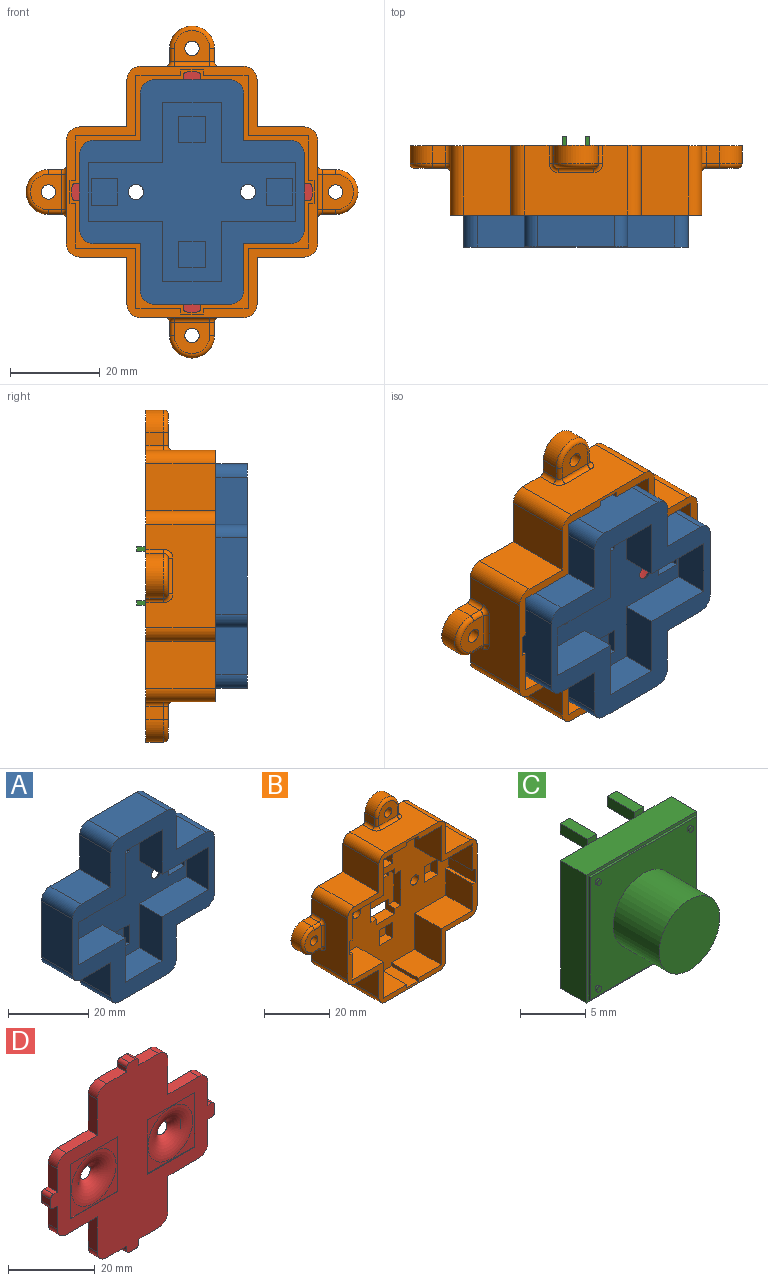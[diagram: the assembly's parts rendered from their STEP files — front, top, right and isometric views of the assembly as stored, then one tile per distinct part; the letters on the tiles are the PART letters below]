
ASSEMBLY  parts=4 mates=3
PART A: 67 faces, bbox 50x11x50 mm
  f0: plane 46x40mm, normal (0,-1,0), area 796.3mm2, adj f14,f15,f16,f17,f18,f19,f20,f21
  f1: plane 50x50mm, normal (0,1,0), area 1281.2mm2, adj f2,f3,f4,f5,f6,f7,f8,f9
  f2: plane 11x10.5mm, normal (0,0,1), area 115.5mm2, adj f1,f13,f26,f27
  f3: plane 17x11mm, normal (-1,0,0), area 187mm2, adj f1,f26,f27,f28
  f4: plane 11x10.5mm, normal (0,0,-1), area 115.5mm2, adj f1,f5,f26,f28
  f5: plane 11x10.5mm, normal (-1,0,0), area 115.5mm2, adj f1,f4,f26,f29
  f6: plane 17x11mm, normal (0,0,-1), area 187mm2, adj f1,f26,f29,f30
  f7: plane 11x10.5mm, normal (1,0,0), area 115.5mm2, adj f1,f8,f26,f30
  f8: plane 11x10.5mm, normal (0,0,-1), area 115.5mm2, adj f1,f7,f26,f31
  f9: plane 17x11mm, normal (1,0,0), area 187mm2, adj f1,f26,f31,f32
  f10: plane 11x10.5mm, normal (0,0,1), area 115.5mm2, adj f1,f11,f26,f32
  f11: plane 11x10.5mm, normal (1,0,0), area 115.5mm2, adj f1,f10,f26,f33
  f12: plane 17x11mm, normal (0,0,1), area 187mm2, adj f1,f26,f33,f34
  f13: plane 11x10.5mm, normal (-1,0,0), area 115.5mm2, adj f1,f2,f26,f34
  f14: plane 13.5x8mm, normal (1,0,0), area 108mm2, adj f0,f15,f25,f26
  f15: plane 13x8mm, normal (0,0,-1), area 104mm2, adj f0,f14,f16,f26
  f16: plane 13.5x8mm, normal (-1,0,0), area 108mm2, adj f0,f15,f17,f26
  f17: plane 16.5x8mm, normal (0,0,-1), area 132mm2, adj f0,f16,f18,f26
  f18: plane 13x8mm, normal (-1,0,0), area 104mm2, adj f0,f17,f19,f26
  f19: plane 16.5x8mm, normal (0,0,1), area 132mm2, adj f0,f18,f20,f26
  f20: plane 13.5x8mm, normal (-1,0,0), area 108mm2, adj f0,f19,f21,f26
  f21: plane 13x8mm, normal (0,0,1), area 104mm2, adj f0,f20,f22,f26
  f22: plane 13.5x8mm, normal (1,0,0), area 108mm2, adj f0,f21,f23,f26
  f23: plane 16.5x8mm, normal (0,0,1), area 132mm2, adj f0,f22,f24,f26
  f24: plane 13x8mm, normal (1,0,0), area 104mm2, adj f0,f23,f25,f26
  f25: plane 16.5x8mm, normal (0,0,-1), area 132mm2, adj f0,f14,f24,f26
  f26: plane 50x50mm, normal (0,-1,0), area 806.5mm2, adj f2,f3,f4,f5,f6,f7,f8,f9
  f27: cylinder r=3mm len=11mm, axis (0,1,0), area 51.8mm2, adj f1,f2,f3,f26
  f28: cylinder r=3mm len=11mm, axis (0,1,0), area 51.8mm2, adj f1,f3,f4,f26
  f29: cylinder r=3mm len=11mm, axis (0,1,0), area 51.8mm2, adj f1,f5,f6,f26
  f30: cylinder r=3mm len=11mm, axis (0,1,0), area 51.8mm2, adj f1,f6,f7,f26
  f31: cylinder r=3mm len=11mm, axis (0,1,0), area 51.8mm2, adj f1,f8,f9,f26
  f32: cylinder r=3mm len=11mm, axis (0,1,0), area 51.8mm2, adj f1,f9,f10,f26
  f33: cylinder r=3mm len=11mm, axis (0,1,0), area 51.8mm2, adj f1,f11,f12,f26
  f34: cylinder r=3mm len=11mm, axis (0,1,0), area 51.8mm2, adj f1,f12,f13,f26
  f35: plane 15.4x0.2mm, normal (0,0,-1), area 3.1mm2, adj f1,f36,f38,f39
  f36: plane 15.4x0.2mm, normal (-1,0,0), area 3.1mm2, adj f1,f35,f37,f39
  f37: plane 15.4x0.2mm, normal (0,0,1), area 3.1mm2, adj f1,f36,f38,f39
  f38: plane 15.4x0.2mm, normal (1,0,0), area 3.1mm2, adj f1,f35,f37,f39
  f39: plane 15.4x15.4mm, normal (0,1,0), area 69.7mm2, adj f35,f36,f37,f38,f65
  f40: plane 15.4x0.2mm, normal (0,0,-1), area 3.1mm2, adj f1,f41,f43,f44
  f41: plane 15.4x0.2mm, normal (-1,0,0), area 3.1mm2, adj f1,f40,f42,f44
  f42: plane 15.4x0.2mm, normal (0,0,1), area 3.1mm2, adj f1,f41,f43,f44
  f43: plane 15.4x0.2mm, normal (1,0,0), area 3.1mm2, adj f1,f40,f42,f44
  f44: plane 15.4x15.4mm, normal (0,1,0), area 69.7mm2, adj f40,f41,f42,f43,f66
  f45: plane 5.8x2mm, normal (0,0,1), area 11.6mm2, adj f0,f46,f48,f49
  f46: plane 5.8x2mm, normal (-1,0,0), area 11.6mm2, adj f0,f45,f47,f49
  f47: plane 5.8x2mm, normal (0,0,-1), area 11.6mm2, adj f0,f46,f48,f49
  f48: plane 5.8x2mm, normal (1,0,0), area 11.6mm2, adj f0,f45,f47,f49
  f49: plane 5.8x5.8mm, normal (0,-1,0), area 33.6mm2, adj f45,f46,f47,f48
  f50: plane 5.8x2mm, normal (-1,0,0), area 11.6mm2, adj f0,f51,f53,f54
  f51: plane 5.8x2mm, normal (0,0,-1), area 11.6mm2, adj f0,f50,f52,f54
  f52: plane 5.8x2mm, normal (1,0,0), area 11.6mm2, adj f0,f51,f53,f54
  f53: plane 5.8x2mm, normal (0,0,1), area 11.6mm2, adj f0,f50,f52,f54
  f54: plane 5.8x5.8mm, normal (0,-1,0), area 33.6mm2, adj f50,f51,f52,f53
  f55: plane 5.8x2mm, normal (0,0,-1), area 11.6mm2, adj f0,f56,f58,f59
  f56: plane 5.8x2mm, normal (1,0,0), area 11.6mm2, adj f0,f55,f57,f59
  f57: plane 5.8x2mm, normal (0,0,1), area 11.6mm2, adj f0,f56,f58,f59
  f58: plane 5.8x2mm, normal (-1,0,0), area 11.6mm2, adj f0,f55,f57,f59
  f59: plane 5.8x5.8mm, normal (0,-1,0), area 33.6mm2, adj f55,f56,f57,f58
  f60: plane 5.8x2mm, normal (0,0,1), area 11.6mm2, adj f0,f61,f63,f64
  f61: plane 5.8x2mm, normal (-1,0,0), area 11.6mm2, adj f0,f60,f62,f64
  f62: plane 5.8x2mm, normal (0,0,-1), area 11.6mm2, adj f0,f61,f63,f64
  f63: plane 5.8x2mm, normal (1,0,0), area 11.6mm2, adj f0,f60,f62,f64
  f64: plane 5.8x5.8mm, normal (0,-1,0), area 33.6mm2, adj f60,f61,f62,f63
  f65: torus R=7.3mm, axis (0,1,0), area 174.6mm2, adj f0,f39
  f66: torus R=7.3mm, axis (0,1,0), area 174.6mm2, adj f0,f44
PART B: 140 faces, bbox 74.8x15.5x74.8 mm
  f0: plane 11.5x10mm, normal (0,0,-1), area 115mm2, adj f4,f5,f58,f79
  f1: plane 11.5x10mm, normal (-1,0,0), area 115mm2, adj f4,f5,f61,f69
  f2: plane 11.5x10mm, normal (0,0,1), area 115mm2, adj f4,f5,f64,f71
  f3: plane 11.5x10mm, normal (1,0,0), area 115mm2, adj f4,f5,f67,f74
  f4: plane 56x56mm, normal (0,-1,0), area 392.5mm2, adj f0,f1,f2,f3,f11,f12,f13,f14
  f5: plane 54.4x54.4mm, normal (0,-1,0), area 1645.3mm2, adj f0,f1,f2,f3,f7,f9,f23,f24
  f6: plane 8x1mm, normal (0,0,-1), area 8mm2, adj f10,f25,f27,f35
  f7: plane 4x4mm, normal (1,0,0), area 10mm2, adj f5,f8,f10,f28,f32,f35
  f8: plane 8x1mm, normal (0,0,1), area 8mm2, adj f7,f9,f10,f35
  f9: plane 4x4mm, normal (-1,0,0), area 10mm2, adj f5,f8,f10,f28,f31,f35
  f10: plane 74x74mm, normal (0,1,0), area 2596mm2, adj f6,f7,f8,f9,f11,f12,f13,f14
  f11: plane 23x15.5mm, normal (-1,0,0), area 286.2mm2, adj f4,f10,f80,f83,f124,f126,f128,f130
  f12: plane 15.5x10.5mm, normal (0,0,-1), area 162.8mm2, adj f4,f10,f13,f80
  f13: plane 15.5x10.5mm, normal (-1,0,0), area 162.8mm2, adj f4,f10,f12,f81
  f14: plane 23x15.5mm, normal (0,0,-1), area 286.2mm2, adj f4,f10,f81,f84,f116,f118,f120,f122
  f15: plane 15.5x10.5mm, normal (1,0,0), area 162.8mm2, adj f4,f10,f16,f84
  f16: plane 15.5x10.5mm, normal (0,0,-1), area 162.8mm2, adj f4,f10,f15,f85
  f17: plane 23x15.5mm, normal (1,0,0), area 286.2mm2, adj f4,f10,f85,f86,f108,f110,f112,f114
  f18: plane 15.5x10.5mm, normal (0,0,1), area 162.8mm2, adj f4,f10,f19,f86
  f19: plane 15.5x10.5mm, normal (1,0,0), area 162.7mm2, adj f4,f10,f18,f87
  f20: plane 23x15.5mm, normal (0,0,1), area 286.2mm2, adj f4,f10,f82,f87,f132,f134,f136,f138
  f21: plane 15.5x10.5mm, normal (-1,0,0), area 162.7mm2, adj f4,f10,f22,f82
  f22: plane 15.5x10.5mm, normal (0,0,1), area 162.8mm2, adj f4,f10,f21,f83
  f23: cylinder r=1.7mm len=4mm, axis (0,1,0), area 42.7mm2, adj f5,f10
  f24: cylinder r=1.7mm len=4mm, axis (0,1,0), area 42.7mm2, adj f5,f10
  f25: plane 4x4mm, normal (1,0,0), area 10mm2, adj f5,f6,f10,f26,f34,f35
  f26: plane 8x4mm, normal (0,0,1), area 32mm2, adj f5,f10,f25,f27
  f27: plane 4x4mm, normal (-1,0,0), area 10mm2, adj f5,f6,f10,f26,f29,f35
  f28: plane 8x4mm, normal (0,0,-1), area 32mm2, adj f5,f7,f9,f10
  f29: plane 3x2.5mm, normal (0,0,1), area 7.5mm2, adj f5,f27,f30,f35
  f30: plane 13x3mm, normal (-1,0,0), area 39mm2, adj f5,f29,f31,f35
  f31: plane 3x2.5mm, normal (0,0,-1), area 7.5mm2, adj f5,f9,f30,f35
  f32: plane 3x2.5mm, normal (0,0,-1), area 7.5mm2, adj f5,f7,f33,f35
  f33: plane 13x3mm, normal (1,0,0), area 39mm2, adj f5,f32,f34,f35
  f34: plane 3x2.5mm, normal (0,0,1), area 7.5mm2, adj f5,f25,f33,f35
  f35: plane 13x13mm, normal (0,-1,0), area 137mm2, adj f6,f7,f8,f9,f25,f27,f29,f30
  f36: plane 5.8x3mm, normal (1,0,0), area 17.4mm2, adj f5,f37,f39,f40
  f37: plane 5.8x3mm, normal (0,0,1), area 17.4mm2, adj f5,f36,f38,f40
  f38: plane 5.8x3mm, normal (-1,0,0), area 17.4mm2, adj f5,f37,f39,f40
  f39: plane 5.8x3mm, normal (0,0,-1), area 17.4mm2, adj f5,f36,f38,f40
  f40: plane 5.8x5.8mm, normal (0,-1,0), area 33.6mm2, adj f36,f37,f38,f39
  f41: plane 5.8x3mm, normal (0,0,-1), area 17.4mm2, adj f5,f42,f44,f45
  f42: plane 5.8x3mm, normal (1,0,0), area 17.4mm2, adj f5,f41,f43,f45
  f43: plane 5.8x3mm, normal (0,0,1), area 17.4mm2, adj f5,f42,f44,f45
  f44: plane 5.8x3mm, normal (-1,0,0), area 17.4mm2, adj f5,f41,f43,f45
  f45: plane 5.8x5.8mm, normal (0,-1,0), area 33.6mm2, adj f41,f42,f43,f44
  f46: plane 5.8x3mm, normal (0,0,-1), area 17.4mm2, adj f5,f47,f49,f50
  f47: plane 5.8x3mm, normal (1,0,0), area 17.4mm2, adj f5,f46,f48,f50
  f48: plane 5.8x3mm, normal (0,0,1), area 17.4mm2, adj f5,f47,f49,f50
  f49: plane 5.8x3mm, normal (-1,0,0), area 17.4mm2, adj f5,f46,f48,f50
  f50: plane 5.8x5.8mm, normal (0,-1,0), area 33.6mm2, adj f46,f47,f48,f49
  f51: plane 5.8x3mm, normal (-1,0,0), area 17.4mm2, adj f5,f52,f54,f55
  f52: plane 5.8x3mm, normal (0,0,-1), area 17.4mm2, adj f5,f51,f53,f55
  f53: plane 5.8x3mm, normal (1,0,0), area 17.4mm2, adj f5,f52,f54,f55
  f54: plane 5.8x3mm, normal (0,0,1), area 17.4mm2, adj f5,f51,f53,f55
  f55: plane 5.8x5.8mm, normal (0,-1,0), area 33.6mm2, adj f51,f52,f53,f54
  f56: plane 13.5x11.5mm, normal (1,0,0), area 155.2mm2, adj f4,f5,f57,f67
  f57: plane 11.5x10mm, normal (0,0,-1), area 115mm2, adj f4,f5,f56,f78
  f58: plane 13.5x11.5mm, normal (-1,0,0), area 155.2mm2, adj f0,f4,f5,f59
  f59: plane 13.5x11.5mm, normal (0,0,-1), area 155.3mm2, adj f4,f5,f58,f60
  f60: plane 11.5x10mm, normal (-1,0,0), area 115mm2, adj f4,f5,f59,f68
  f61: plane 13.5x11.5mm, normal (0,0,1), area 155.3mm2, adj f1,f4,f5,f62
  f62: plane 13.5x11.5mm, normal (-1,0,0), area 155.2mm2, adj f4,f5,f61,f63
  f63: plane 11.5x10mm, normal (0,0,1), area 115mm2, adj f4,f5,f62,f73
  f64: plane 13.5x11.5mm, normal (1,0,0), area 155.2mm2, adj f2,f4,f5,f65
  f65: plane 13.5x11.5mm, normal (0,0,1), area 155.3mm2, adj f4,f5,f64,f66
  f66: plane 11.5x10mm, normal (1,0,0), area 115mm2, adj f4,f5,f65,f76
  f67: plane 13.5x11.5mm, normal (0,0,-1), area 155.3mm2, adj f3,f4,f5,f56
  f68: plane 11.5x1.2mm, normal (0,0,-1), area 13.8mm2, adj f4,f5,f60,f70
  f69: plane 11.5x1.2mm, normal (0,0,1), area 13.8mm2, adj f1,f4,f5,f70
  f70: plane 11.5x5mm, normal (-1,0,0), area 57.5mm2, adj f4,f5,f68,f69
  f71: plane 11.5x1.2mm, normal (1,0,0), area 13.8mm2, adj f2,f4,f5,f72
  f72: plane 11.5x5mm, normal (0,0,1), area 57.5mm2, adj f4,f5,f71,f73
  f73: plane 11.5x1.2mm, normal (-1,0,0), area 13.8mm2, adj f4,f5,f63,f72
  f74: plane 11.5x1.2mm, normal (0,0,-1), area 13.8mm2, adj f3,f4,f5,f75
  f75: plane 11.5x5mm, normal (1,0,0), area 57.5mm2, adj f4,f5,f74,f76
  f76: plane 11.5x1.2mm, normal (0,0,1), area 13.8mm2, adj f4,f5,f66,f75
  f77: plane 11.5x5mm, normal (0,0,-1), area 57.5mm2, adj f4,f5,f78,f79
  f78: plane 11.5x1.2mm, normal (1,0,0), area 13.8mm2, adj f4,f5,f57,f77
  f79: plane 11.5x1.2mm, normal (-1,0,0), area 13.8mm2, adj f0,f4,f5,f77
  f80: cylinder r=3mm len=15.5mm, axis (0,1,0), area 73mm2, adj f4,f10,f11,f12
  f81: cylinder r=3mm len=15.5mm, axis (0,1,0), area 73mm2, adj f4,f10,f13,f14
  f82: cylinder r=3mm len=15.5mm, axis (0,1,0), area 73mm2, adj f4,f10,f20,f21
  f83: cylinder r=3mm len=15.5mm, axis (0,1,0), area 73mm2, adj f4,f10,f11,f22
  f84: cylinder r=3mm len=15.5mm, axis (0,1,0), area 73mm2, adj f4,f10,f14,f15
  f85: cylinder r=3mm len=15.5mm, axis (0,1,0), area 73mm2, adj f4,f10,f16,f17
  f86: cylinder r=3mm len=15.5mm, axis (0,1,0), area 73mm2, adj f4,f10,f17,f18
  f87: cylinder r=3mm len=15.5mm, axis (0,1,0), area 73mm2, adj f4,f10,f19,f20
  f88: plane 4x3mm, normal (0,0,1), area 12mm2, adj f10,f89,f129,f131
  f89: cylinder r=5mm len=10mm, axis (0,1,0), area 62.8mm2, adj f10,f88,f90,f127
  f90: plane 4x3mm, normal (0,0,-1), area 12mm2, adj f10,f89,f124,f125
  f91: cylinder r=1.6mm len=5mm, axis (0,1,0), area 50.3mm2, adj f10,f92
  f92: plane 8x7mm, normal (0,-1,0), area 41.1mm2, adj f91,f125,f127,f128,f129
  f93: plane 4x3mm, normal (-1,0,0), area 12mm2, adj f10,f94,f121,f123
  f94: cylinder r=5mm len=10mm, axis (0,1,0), area 62.8mm2, adj f10,f93,f95,f119
  f95: plane 4x3mm, normal (1,0,0), area 12mm2, adj f10,f94,f116,f117
  f96: cylinder r=1.6mm len=5mm, axis (0,1,0), area 50.3mm2, adj f10,f97
  f97: plane 8x7mm, normal (0,-1,0), area 41.1mm2, adj f96,f117,f119,f120,f121
  f98: plane 4x3mm, normal (0,0,-1), area 12mm2, adj f10,f99,f113,f115
  f99: cylinder r=5mm len=10mm, axis (0,1,0), area 62.8mm2, adj f10,f98,f100,f111
  f100: plane 4x3mm, normal (0,0,1), area 12mm2, adj f10,f99,f108,f109
  f101: cylinder r=1.6mm len=5mm, axis (0,1,0), area 50.3mm2, adj f10,f102
  f102: plane 8x7mm, normal (0,-1,0), area 41.1mm2, adj f101,f109,f111,f112,f113
  f103: plane 4x3mm, normal (1,0,0), area 12mm2, adj f10,f104,f137,f139
  f104: cylinder r=5mm len=10mm, axis (0,1,0), area 62.8mm2, adj f10,f103,f105,f135
  f105: plane 4x3mm, normal (-1,0,0), area 12mm2, adj f10,f104,f132,f133
  f106: cylinder r=1.6mm len=5mm, axis (0,1,0), area 50.3mm2, adj f10,f107
  f107: plane 8x7mm, normal (0,-1,0), area 41.1mm2, adj f106,f133,f135,f136,f137
  f108: cylinder r=1mm len=4mm, axis (0,-1,0), area 6.3mm2, adj f10,f17,f100,f110
  f109: cylinder r=1mm len=3mm, axis (1,0,0), area 4.7mm2, adj f100,f102,f110,f111
  f110: torus R=2mm, axis (-1,0,0), area 3.4mm2, adj f17,f108,f109,f112
  f111: torus R=4mm, axis (0,-1,0), area 22.9mm2, adj f99,f102,f109,f113
  f112: cylinder r=1mm len=8mm, axis (0,0,1), area 12.6mm2, adj f17,f102,f110,f114
  f113: cylinder r=1mm len=3mm, axis (-1,0,0), area 4.7mm2, adj f98,f102,f111,f114
  f114: torus R=2mm, axis (-1,0,0), area 3.4mm2, adj f17,f112,f113,f115
  f115: cylinder r=1mm len=4mm, axis (0,1,0), area 6.3mm2, adj f10,f17,f98,f114
  f116: cylinder r=1mm len=4mm, axis (0,-1,0), area 6.3mm2, adj f10,f14,f95,f118
  f117: cylinder r=1mm len=3mm, axis (0,0,-1), area 4.7mm2, adj f95,f97,f118,f119
  f118: torus R=2mm, axis (0,0,1), area 3.4mm2, adj f14,f116,f117,f120
  f119: torus R=4mm, axis (0,-1,0), area 22.9mm2, adj f94,f97,f117,f121
  f120: cylinder r=1mm len=8mm, axis (1,0,0), area 12.6mm2, adj f14,f97,f118,f122
  f121: cylinder r=1mm len=3mm, axis (0,0,1), area 4.7mm2, adj f93,f97,f119,f122
  f122: torus R=2mm, axis (0,0,1), area 3.4mm2, adj f14,f120,f121,f123
  f123: cylinder r=1mm len=4mm, axis (0,1,0), area 6.3mm2, adj f10,f14,f93,f122
  f124: cylinder r=1mm len=4mm, axis (0,-1,0), area 6.3mm2, adj f10,f11,f90,f126
  f125: cylinder r=1mm len=3mm, axis (-1,0,0), area 4.7mm2, adj f90,f92,f126,f127
  f126: torus R=2mm, axis (1,0,0), area 3.4mm2, adj f11,f124,f125,f128
  f127: torus R=4mm, axis (0,-1,0), area 22.9mm2, adj f89,f92,f125,f129
  f128: cylinder r=1mm len=8mm, axis (0,0,-1), area 12.6mm2, adj f11,f92,f126,f130
  f129: cylinder r=1mm len=3mm, axis (1,0,0), area 4.7mm2, adj f88,f92,f127,f130
  f130: torus R=2mm, axis (1,0,0), area 3.4mm2, adj f11,f128,f129,f131
  f131: cylinder r=1mm len=4mm, axis (0,1,0), area 6.3mm2, adj f10,f11,f88,f130
  f132: cylinder r=1mm len=4mm, axis (0,-1,0), area 6.3mm2, adj f10,f20,f105,f134
  f133: cylinder r=1mm len=3mm, axis (0,0,1), area 4.7mm2, adj f105,f107,f134,f135
  f134: torus R=2mm, axis (0,0,-1), area 3.4mm2, adj f20,f132,f133,f136
  f135: torus R=4mm, axis (0,-1,0), area 22.9mm2, adj f104,f107,f133,f137
  f136: cylinder r=1mm len=8mm, axis (-1,0,0), area 12.6mm2, adj f20,f107,f134,f138
  f137: cylinder r=1mm len=3mm, axis (0,0,-1), area 4.7mm2, adj f103,f107,f135,f138
  f138: torus R=2mm, axis (0,0,-1), area 3.4mm2, adj f20,f136,f137,f139
  f139: cylinder r=1mm len=4mm, axis (0,1,0), area 6.3mm2, adj f10,f20,f103,f138
PART C: 45 faces, bbox 12x11x13 mm
  f0: plane 12x12mm, normal (0,1,0), area 142mm2, adj f17,f18,f19,f20,f22,f23,f24,f27
  f1: plane 11.5x11.5mm, normal (0,-1,0), area 97.3mm2, adj f2,f4,f6,f8,f10,f12,f13,f14
  f2: cylinder r=3.3mm len=6.6mm, axis (0,1,0), area 103.7mm2, adj f1,f3
  f3: plane 6.6x6.6mm, normal (0,-1,0), area 34.2mm2, adj f2
  f4: cylinder r=0.25mm len=0.5mm, axis (0,1,0), area 0.3mm2, adj f1,f5
  f5: plane 0.5x0.5mm, normal (0,-1,0), area 0.2mm2, adj f4
  f6: cylinder r=0.25mm len=0.5mm, axis (0,1,0), area 0.3mm2, adj f1,f7
  f7: plane 0.5x0.5mm, normal (0,-1,0), area 0.2mm2, adj f6
  f8: cylinder r=0.25mm len=0.5mm, axis (0,1,0), area 0.3mm2, adj f1,f9
  f9: plane 0.5x0.5mm, normal (0,-1,0), area 0.2mm2, adj f8
  f10: cylinder r=0.25mm len=0.5mm, axis (0,1,0), area 0.3mm2, adj f1,f11
  f11: plane 0.5x0.5mm, normal (0,-1,0), area 0.2mm2, adj f10
  f12: plane 11.5x0.2mm, normal (-1,0,0), area 2.3mm2, adj f1,f13,f15,f16
  f13: plane 11.5x0.2mm, normal (0,0,1), area 2.3mm2, adj f1,f12,f14,f16
  f14: plane 11.5x0.2mm, normal (1,0,0), area 2.3mm2, adj f1,f13,f15,f16
  f15: plane 11.5x0.2mm, normal (0,0,-1), area 2.3mm2, adj f1,f12,f14,f16
  f16: plane 12x12mm, normal (0,-1,0), area 11.8mm2, adj f12,f13,f14,f15,f17,f18,f19,f20
  f17: plane 12x2.8mm, normal (-1,0,0), area 33.6mm2, adj f0,f16,f18,f20
  f18: plane 12x2.8mm, normal (0,0,1), area 33.6mm2, adj f0,f16,f17,f19,f26,f32
  f19: plane 12x2.8mm, normal (1,0,0), area 33.6mm2, adj f0,f16,f18,f20
  f20: plane 12x2.8mm, normal (0,0,-1), area 33.6mm2, adj f0,f16,f17,f19,f33,f39
  f21: plane 3x1mm, normal (0,0,1), area 3mm2, adj f22,f24,f25,f26
  f22: plane 3x1mm, normal (1,0,0), area 3mm2, adj f0,f21,f23,f25,f26
  f23: plane 3x1mm, normal (0,0,-1), area 3mm2, adj f0,f22,f24,f25
  f24: plane 3x1mm, normal (-1,0,0), area 3mm2, adj f0,f21,f23,f25,f26
  f25: plane 1x1mm, normal (0,1,0), area 1mm2, adj f21,f22,f23,f24
  f26: plane 1x0.5mm, normal (0,-1,0), area 0.5mm2, adj f18,f21,f22,f24
  f27: plane 3x1mm, normal (0,0,-1), area 3mm2, adj f0,f28,f30,f31
  f28: plane 3x1mm, normal (-1,0,0), area 3mm2, adj f0,f27,f29,f31,f32
  f29: plane 3x1mm, normal (0,0,1), area 3mm2, adj f28,f30,f31,f32
  f30: plane 3x1mm, normal (1,0,0), area 3mm2, adj f0,f27,f29,f31,f32
  f31: plane 1x1mm, normal (0,1,0), area 1mm2, adj f27,f28,f29,f30
  f32: plane 1x0.5mm, normal (0,-1,0), area 0.5mm2, adj f18,f28,f29,f30
  f33: plane 1x0.5mm, normal (0,-1,0), area 0.5mm2, adj f20,f34,f35,f36
  f34: plane 3x1mm, normal (1,0,0), area 3mm2, adj f0,f33,f35,f37,f38
  f35: plane 3x1mm, normal (0,0,-1), area 3mm2, adj f33,f34,f36,f38
  f36: plane 3x1mm, normal (-1,0,0), area 3mm2, adj f0,f33,f35,f37,f38
  f37: plane 3x1mm, normal (0,0,1), area 3mm2, adj f0,f34,f36,f38
  f38: plane 1x1mm, normal (0,1,0), area 1mm2, adj f34,f35,f36,f37
  f39: plane 1x0.5mm, normal (0,-1,0), area 0.5mm2, adj f20,f40,f41,f42
  f40: plane 3x1mm, normal (1,0,0), area 3mm2, adj f0,f39,f41,f43,f44
  f41: plane 3x1mm, normal (0,0,-1), area 3mm2, adj f39,f40,f42,f44
  f42: plane 3x1mm, normal (-1,0,0), area 3mm2, adj f0,f39,f41,f43,f44
  f43: plane 3x1mm, normal (0,0,1), area 3mm2, adj f0,f40,f42,f44
  f44: plane 1x1mm, normal (0,1,0), area 1mm2, adj f40,f41,f42,f43
PART D: 78 faces, bbox 53.5x7.2x53.5 mm
  f0: plane 53.5x53.5mm, normal (0,-1,0), area 1273.3mm2, adj f2,f3,f4,f5,f6,f7,f8,f9
  f1: plane 53.5x53.5mm, normal (0,1,0), area 1594.9mm2, adj f2,f3,f4,f5,f6,f7,f8,f9
  f2: plane 6.5x3mm, normal (0,0,-1), area 19.5mm2, adj f0,f1,f3,f33
  f3: plane 3x1.2mm, normal (-1,0,0), area 3.6mm2, adj f0,f1,f2,f74
  f4: plane 3x2mm, normal (0,0,-1), area 6mm2, adj f0,f1,f74,f75
  f5: plane 3x1.2mm, normal (1,0,0), area 3.6mm2, adj f0,f1,f6,f75
  f6: plane 6.5x3mm, normal (0,0,-1), area 19.5mm2, adj f0,f1,f5,f34
  f7: plane 10.05x3mm, normal (1,0,0), area 30.1mm2, adj f0,f1,f8,f34
  f8: plane 10.05x3mm, normal (0,0,-1), area 30.1mm2, adj f0,f1,f7,f35
  f9: plane 6.5x3mm, normal (1,0,0), area 19.5mm2, adj f0,f1,f10,f35
  f10: plane 3x1.2mm, normal (0,0,-1), area 3.6mm2, adj f0,f1,f9,f72
  f11: plane 3x2mm, normal (1,0,0), area 6mm2, adj f0,f1,f72,f73
  f12: plane 3x1.2mm, normal (0,0,1), area 3.6mm2, adj f0,f1,f13,f73
  f13: plane 6.5x3mm, normal (1,0,0), area 19.5mm2, adj f0,f1,f12,f36
  f14: plane 10.05x3mm, normal (0,0,1), area 30.1mm2, adj f0,f1,f15,f36
  f15: plane 10.05x3mm, normal (1,0,0), area 30.1mm2, adj f0,f1,f14,f37
  f16: plane 6.5x3mm, normal (0,0,1), area 19.5mm2, adj f0,f1,f17,f37
  f17: plane 3x1.2mm, normal (1,0,0), area 3.6mm2, adj f0,f1,f16,f70
  f18: plane 3x2mm, normal (0,0,1), area 6mm2, adj f0,f1,f70,f71
  f19: plane 3x1.2mm, normal (-1,0,0), area 3.6mm2, adj f0,f1,f20,f71
  f20: plane 6.5x3mm, normal (0,0,1), area 19.5mm2, adj f0,f1,f19,f30
  f21: plane 10.05x3mm, normal (-1,0,0), area 30.1mm2, adj f0,f1,f22,f30
  f22: plane 10.05x3mm, normal (0,0,1), area 30.1mm2, adj f0,f1,f21,f31
  f23: plane 6.5x3mm, normal (-1,0,0), area 19.5mm2, adj f0,f1,f24,f31
  f24: plane 3x1.2mm, normal (0,0,1), area 3.6mm2, adj f0,f1,f23,f76
  f25: plane 3x2mm, normal (-1,0,0), area 6mm2, adj f0,f1,f76,f77
  f26: plane 3x1.2mm, normal (0,0,-1), area 3.6mm2, adj f0,f1,f27,f77
  f27: plane 6.5x3mm, normal (-1,0,0), area 19.5mm2, adj f0,f1,f26,f32
  f28: plane 10.05x3mm, normal (0,0,-1), area 30.1mm2, adj f0,f1,f29,f32
  f29: plane 10.05x3mm, normal (-1,0,0), area 30.1mm2, adj f0,f1,f28,f33
  f30: cylinder r=3mm len=3mm, axis (0,1,0), area 14.1mm2, adj f0,f1,f20,f21
  f31: cylinder r=3mm len=3mm, axis (0,1,0), area 14.1mm2, adj f0,f1,f22,f23
  f32: cylinder r=3mm len=3mm, axis (0,1,0), area 14.1mm2, adj f0,f1,f27,f28
  f33: cylinder r=3mm len=3mm, axis (0,1,0), area 14.1mm2, adj f0,f1,f2,f29
  f34: cylinder r=3mm len=3mm, axis (0,1,0), area 14.1mm2, adj f0,f1,f6,f7
  f35: cylinder r=3mm len=3mm, axis (0,1,0), area 14.1mm2, adj f0,f1,f8,f9
  f36: cylinder r=3mm len=3mm, axis (0,1,0), area 14.1mm2, adj f0,f1,f13,f14
  f37: cylinder r=3mm len=3mm, axis (0,1,0), area 14.1mm2, adj f0,f1,f15,f16
  f38: plane 5.8x2mm, normal (0,0,1), area 11.6mm2, adj f1,f39,f41,f42
  f39: plane 5.8x2mm, normal (1,0,0), area 11.6mm2, adj f1,f38,f40,f42
  f40: plane 5.8x2mm, normal (0,0,-1), area 11.6mm2, adj f1,f39,f41,f42
  f41: plane 5.8x2mm, normal (-1,0,0), area 11.6mm2, adj f1,f38,f40,f42
  f42: plane 5.8x5.8mm, normal (0,1,0), area 33.6mm2, adj f38,f39,f40,f41
  f43: plane 5.8x2mm, normal (1,0,0), area 11.6mm2, adj f1,f44,f46,f47
  f44: plane 5.8x2mm, normal (0,0,-1), area 11.6mm2, adj f1,f43,f45,f47
  f45: plane 5.8x2mm, normal (-1,0,0), area 11.6mm2, adj f1,f44,f46,f47
  f46: plane 5.8x2mm, normal (0,0,1), area 11.6mm2, adj f1,f43,f45,f47
  f47: plane 5.8x5.8mm, normal (0,1,0), area 33.6mm2, adj f43,f44,f45,f46
  f48: plane 5.8x2mm, normal (0,0,-1), area 11.6mm2, adj f1,f49,f51,f52
  f49: plane 5.8x2mm, normal (-1,0,0), area 11.6mm2, adj f1,f48,f50,f52
  f50: plane 5.8x2mm, normal (0,0,1), area 11.6mm2, adj f1,f49,f51,f52
  f51: plane 5.8x2mm, normal (1,0,0), area 11.6mm2, adj f1,f48,f50,f52
  f52: plane 5.8x5.8mm, normal (0,1,0), area 33.6mm2, adj f48,f49,f50,f51
  f53: plane 5.8x2mm, normal (0,0,-1), area 11.6mm2, adj f1,f54,f56,f57
  f54: plane 5.8x2mm, normal (-1,0,0), area 11.6mm2, adj f1,f53,f55,f57
  f55: plane 5.8x2mm, normal (0,0,1), area 11.6mm2, adj f1,f54,f56,f57
  f56: plane 5.8x2mm, normal (1,0,0), area 11.6mm2, adj f1,f53,f55,f57
  f57: plane 5.8x5.8mm, normal (0,1,0), area 33.6mm2, adj f53,f54,f55,f56
  f58: plane 15.4x0.2mm, normal (0,0,-1), area 3.1mm2, adj f0,f59,f61,f62
  f59: plane 15.4x0.2mm, normal (1,0,0), area 3.1mm2, adj f0,f58,f60,f62
  f60: plane 15.4x0.2mm, normal (0,0,1), area 3.1mm2, adj f0,f59,f61,f62
  f61: plane 15.4x0.2mm, normal (-1,0,0), area 3.1mm2, adj f0,f58,f60,f62
  f62: plane 15.4x15.4mm, normal (0,-1,0), area 69.7mm2, adj f58,f59,f60,f61,f68
  f63: plane 15.4x0.2mm, normal (0,0,-1), area 3.1mm2, adj f0,f64,f66,f67
  f64: plane 15.4x0.2mm, normal (1,0,0), area 3.1mm2, adj f0,f63,f65,f67
  f65: plane 15.4x0.2mm, normal (0,0,1), area 3.1mm2, adj f0,f64,f66,f67
  f66: plane 15.4x0.2mm, normal (-1,0,0), area 3.1mm2, adj f0,f63,f65,f67
  f67: plane 15.4x15.4mm, normal (0,-1,0), area 69.7mm2, adj f63,f64,f65,f66,f69
  f68: torus R=7.3mm, axis (0,-1,0), area 174.6mm2, adj f1,f62
  f69: torus R=7.3mm, axis (0,-1,0), area 174.6mm2, adj f1,f67
  f70: cylinder r=1mm len=3mm, axis (0,1,0), area 4.7mm2, adj f0,f1,f17,f18
  f71: cylinder r=1mm len=3mm, axis (0,-1,0), area 4.7mm2, adj f0,f1,f18,f19
  f72: cylinder r=1mm len=3mm, axis (0,1,0), area 4.7mm2, adj f0,f1,f10,f11
  f73: cylinder r=1mm len=3mm, axis (0,-1,0), area 4.7mm2, adj f0,f1,f11,f12
  f74: cylinder r=1mm len=3mm, axis (0,1,0), area 4.7mm2, adj f0,f1,f3,f4
  f75: cylinder r=1mm len=3mm, axis (0,-1,0), area 4.7mm2, adj f0,f1,f4,f5
  f76: cylinder r=1mm len=3mm, axis (0,-1,0), area 4.7mm2, adj f0,f1,f24,f25
  f77: cylinder r=1mm len=3mm, axis (0,1,0), area 4.7mm2, adj f0,f1,f25,f26
PLACE A t=(14.15,-8.1,65.89)mm
PLACE B t=(13.15,3.5,54.89)mm
PLACE C t=(-24.24,2.5,52.2)mm
PLACE D t=(43.02,-5.5,50.79)mm
MATE fastened B.f35 <-> C.f2  axis (0,-1,0) through (-13.12,2.5,64.77)mm
MATE fastened A.f66 <-> D.f68  axis (0,1,0) through (-0.62,-8.3,64.77)mm
MATE fastened D.f1 <-> C.f2  axis (0,1,0) through (-13.12,-5.5,64.77)mm
